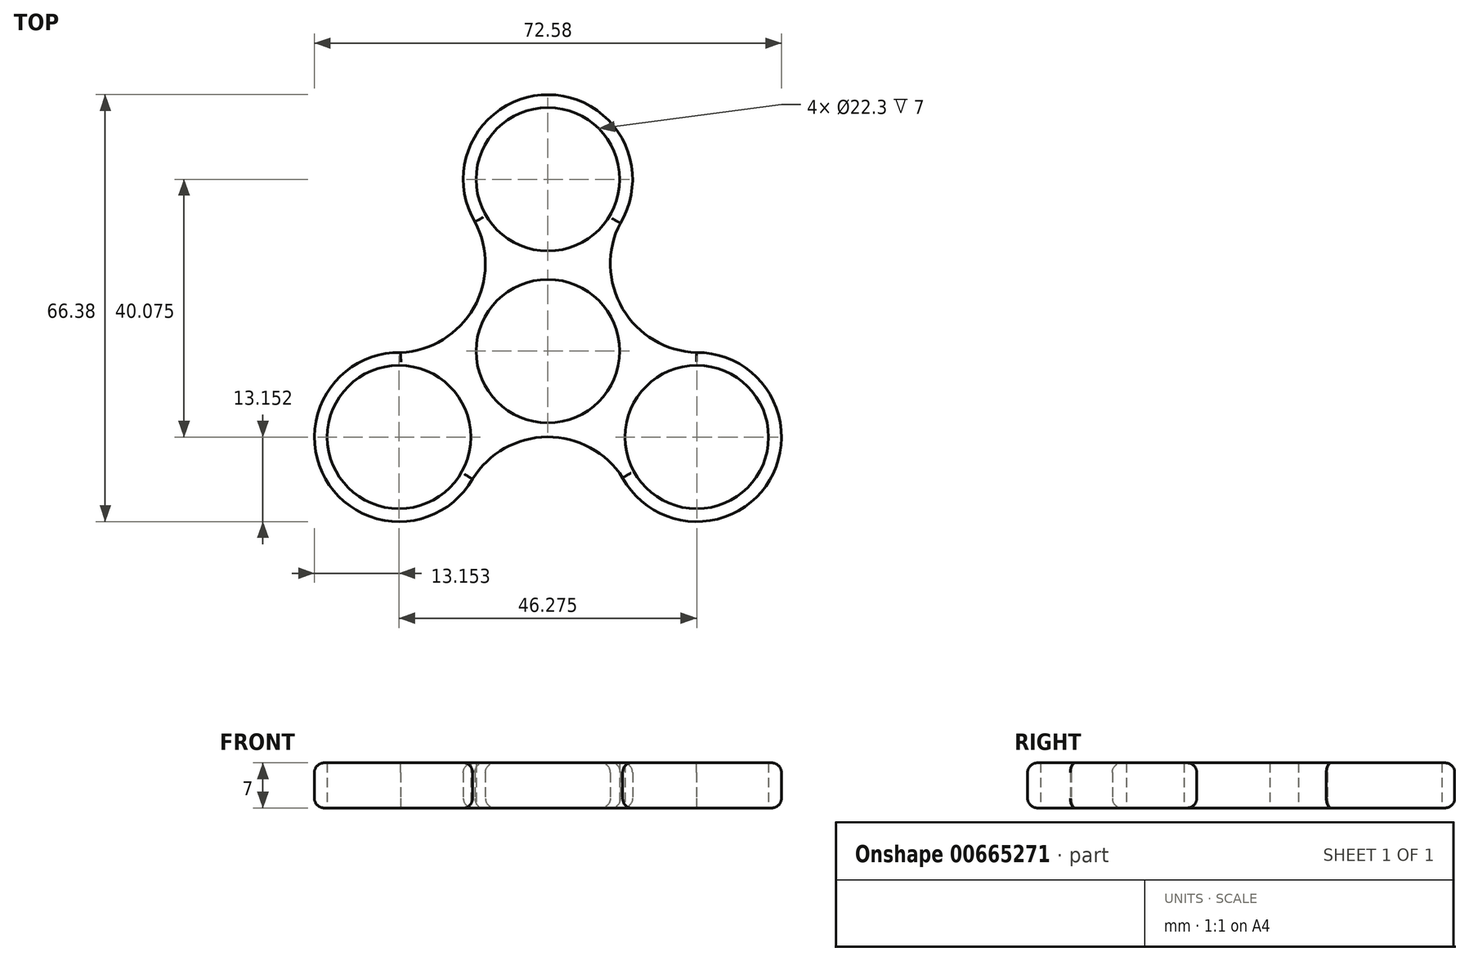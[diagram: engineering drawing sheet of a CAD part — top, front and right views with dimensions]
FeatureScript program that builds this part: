
annotation { "Feature Type Name" : "Feature", "Feature Type Description" : "" }
export const myFeature = defineFeature(function(context is Context, id is Id, definition is map)
    precondition{}
    {
        {
            var Q0;
            Q0=qCreatedBy(makeId("Top.planeOp"),FACE);
            var sketch = newSketch(context, id + "F0", { "sketchPlane" : qUnion([Q0])});
            skCircle(sketch, "E0", {"center": v(0, 0) * mm, "radius": 11.15 * mm});
            skCircle(sketch, "E1", {"center": v(0, 26.72) * mm, "radius": 11.15 * mm});
            skArc(sketch, "E2", {"start": v(11.25, 19.91) * mm, "mid": v(0.1, 39.87) * mm, "end": v(-11.35, 20.08) * mm});
            skCircle(sketch, "E3.1.0", {"center": v(-23.14, -13.36) * mm, "radius": 11.15 * mm});
            skArc(sketch, "E3.1.1", {"start": v(-22.87, -0.21) * mm, "mid": v(-34.58, -19.85) * mm, "end": v(-11.72, -19.88) * mm});
            skCircle(sketch, "E3.2.0", {"center": v(23.14, -13.36) * mm, "radius": 11.15 * mm});
            skArc(sketch, "E3.2.1", {"start": v(11.62, -19.7) * mm, "mid": v(34.47, -20.02) * mm, "end": v(23.07, -0.2) * mm});
            skArc(sketch, "E4", {"start": v(11.25, 19.91) * mm, "mid": v(11.6, 6.59) * mm, "end": v(23.07, -0.2) * mm});
            skArc(sketch, "E5.1.0", {"start": v(-22.87, -0.21) * mm, "mid": v(-11.5, 6.76) * mm, "end": v(-11.35, 20.08) * mm});
            skArc(sketch, "E5.2.0", {"start": v(11.62, -19.7) * mm, "mid": v(-0.1, -13.34) * mm, "end": v(-11.72, -19.88) * mm});
            skSolve(sketch);
        }
        {
            var Q0;
            Q0=makeQuery(id+"F0.imprint","IMPRINT",FACE,{"disambiguationData":[TD([[makeQuery(id+"F0.imprint","IMPRINT",EDGE,{"derivedFrom":sQuery(id+"F0.wireOp",EDGE,"E0")}),-1.0]])]});
            extrude(context, id + "F1", {"entities" : qUnion([Q0]), "depth" : 7 * mm, "offsetDistance" : 25 * mm});
        }
        {
            var Q0;
            Q0=makeQuery(id+"F1.opExtrude","CAP_EDGE",EDGE,{"disambiguationData":[OSD([sQuery(id+"F0.wireOp",EDGE,"E5.1.0")])],"isStart":true});
            var Q1;
            Q1=makeQuery(id+"F1.opExtrude","CAP_EDGE",EDGE,{"disambiguationData":[OSD([sQuery(id+"F0.wireOp",EDGE,"E3.1.1")])],"isStart":true});
            var Q2;
            Q2=makeQuery(id+"F1.opExtrude","CAP_EDGE",EDGE,{"disambiguationData":[OSD([sQuery(id+"F0.wireOp",EDGE,"E5.2.0")])],"isStart":true});
            var Q3;
            Q3=makeQuery(id+"F1.opExtrude","CAP_EDGE",EDGE,{"disambiguationData":[OSD([sQuery(id+"F0.wireOp",EDGE,"E3.2.1")])],"isStart":true});
            var Q4;
            Q4=makeQuery(id+"F1.opExtrude","CAP_EDGE",EDGE,{"disambiguationData":[OSD([sQuery(id+"F0.wireOp",EDGE,"E4")])],"isStart":true});
            var Q5;
            Q5=makeQuery(id+"F1.opExtrude","CAP_EDGE",EDGE,{"disambiguationData":[OSD([sQuery(id+"F0.wireOp",EDGE,"E2")])],"isStart":true});
            fillet(context, id + "F2", {"entities" : qUnion([Q0, Q1, Q2, Q3, Q4, Q5]), "radius" : 1.5 * mm, "tangentPropagation" : true, "allowEdgeOverflow" : false});
        }
        {
            var Q0;
            Q0=makeQuery(id+"F1.opExtrude","CAP_EDGE",EDGE,{"disambiguationData":[OSD([sQuery(id+"F0.wireOp",EDGE,"E5.1.0")])],"isStart":false});
            var Q1;
            Q1=makeQuery(id+"F1.opExtrude","CAP_EDGE",EDGE,{"disambiguationData":[OSD([sQuery(id+"F0.wireOp",EDGE,"E2")])],"isStart":false});
            var Q2;
            Q2=makeQuery(id+"F1.opExtrude","CAP_EDGE",EDGE,{"disambiguationData":[OSD([sQuery(id+"F0.wireOp",EDGE,"E4")])],"isStart":false});
            var Q3;
            Q3=makeQuery(id+"F1.opExtrude","CAP_EDGE",EDGE,{"disambiguationData":[OSD([sQuery(id+"F0.wireOp",EDGE,"E3.2.1")])],"isStart":false});
            var Q4;
            Q4=makeQuery(id+"F1.opExtrude","CAP_EDGE",EDGE,{"disambiguationData":[OSD([sQuery(id+"F0.wireOp",EDGE,"E5.2.0")])],"isStart":false});
            var Q5;
            Q5=makeQuery(id+"F1.opExtrude","CAP_EDGE",EDGE,{"disambiguationData":[OSD([sQuery(id+"F0.wireOp",EDGE,"E3.1.1")])],"isStart":false});
            fillet(context, id + "F3", {"entities" : qUnion([Q0, Q1, Q2, Q3, Q4, Q5]), "radius" : 1.5 * mm, "tangentPropagation" : true, "allowEdgeOverflow" : false});
        }
    });
